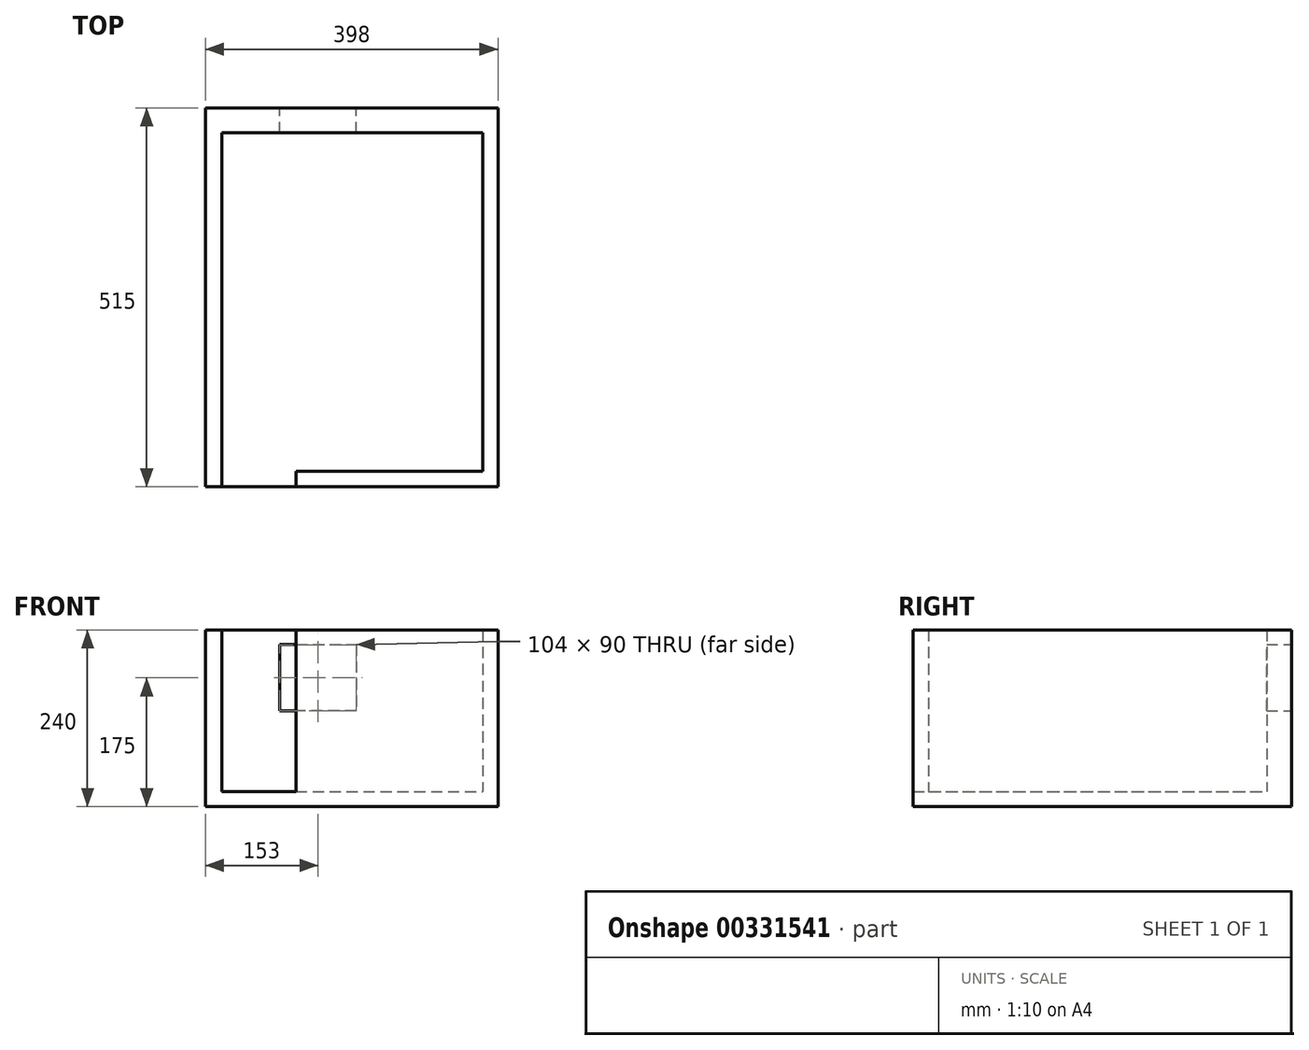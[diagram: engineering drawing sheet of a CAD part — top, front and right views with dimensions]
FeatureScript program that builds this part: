
annotation { "Feature Type Name" : "Feature", "Feature Type Description" : "" }
export const myFeature = defineFeature(function(context is Context, id is Id, definition is map)
    precondition{}
    {
        {
            var Q0;
            Q0=qCreatedBy(makeId("Top.planeOp"),FACE);
            var sketch = newSketch(context, id + "F0", { "sketchPlane" : qUnion([Q0])});
            skLineSegment(sketch, "E0", {"start": v(1313, 440) * mm, "end": v(1313, 406) * mm});
            skLineSegment(sketch, "E1", {"start": v(1313, -267) * mm, "end": v(1313, -301) * mm});
            skLineSegment(sketch, "E2", {"start": v(1313, -301) * mm, "end": v(647, -301) * mm});
            skLineSegment(sketch, "E3", {"start": v(1279, -267) * mm, "end": v(647, -267) * mm});
            skLineSegment(sketch, "E4", {"start": v(1279, 406) * mm, "end": v(688, 406) * mm});
            skLineSegment(sketch, "E5", {"start": v(688, 406) * mm, "end": v(688, -75) * mm});
            skLineSegment(sketch, "E6", {"start": v(688, -75) * mm, "end": v(413, -75) * mm});
            skLineSegment(sketch, "E7", {"start": v(647, -301) * mm, "end": v(647, -267) * mm});
            skLineSegment(sketch, "E8", {"start": v(536, -301) * mm, "end": v(536, -267) * mm});
            skLineSegment(sketch, "E9", {"start": v(536, -267) * mm, "end": v(328, -267) * mm});
            skLineSegment(sketch, "E10", {"start": v(328, -267) * mm, "end": v(328, -407) * mm});
            skLineSegment(sketch, "E11", {"start": v(328, -407) * mm, "end": v(-40, -407) * mm});
            skLineSegment(sketch, "E12", {"start": v(-40, -407) * mm, "end": v(-40, -188) * mm});
            skLineSegment(sketch, "E13", {"start": v(-40, -188) * mm, "end": v(-105, -188) * mm});
            skLineSegment(sketch, "E14", {"start": v(536, -301) * mm, "end": v(362, -301) * mm});
            skLineSegment(sketch, "E15", {"start": v(362, -301) * mm, "end": v(362, -440) * mm});
            skLineSegment(sketch, "E16", {"start": v(-60, -407) * mm, "end": v(-60, -215) * mm});
            skLineSegment(sketch, "E17", {"start": v(-60, -215) * mm, "end": v(-105, -215) * mm});
            skLineSegment(sketch, "E18", {"start": v(-105, -188) * mm, "end": v(-105, -215) * mm});
            skLineSegment(sketch, "E19", {"start": v(-60, -407) * mm, "end": v(-282, -407) * mm});
            skLineSegment(sketch, "E20", {"start": v(-282, -407) * mm, "end": v(-282, -287) * mm});
            skLineSegment(sketch, "E21", {"start": v(-282, -287) * mm, "end": v(-330, -287) * mm});
            skLineSegment(sketch, "E22", {"start": v(-330, -287) * mm, "end": v(-330, -407) * mm});
            skLineSegment(sketch, "E23", {"start": v(-330, -407) * mm, "end": v(-497, -407) * mm});
            skLineSegment(sketch, "E24", {"start": v(-197, -188) * mm, "end": v(-197, -215) * mm});
            skLineSegment(sketch, "E25", {"start": v(-197, -188) * mm, "end": v(-765, -188) * mm});
            skLineSegment(sketch, "E26", {"start": v(-197, -215) * mm, "end": v(-497, -215) * mm});
            skLineSegment(sketch, "E27", {"start": v(-497, -215) * mm, "end": v(-497, -231) * mm});
            skLineSegment(sketch, "E28", {"start": v(-497, -231) * mm, "end": v(-497, -293) * mm});
            skLineSegment(sketch, "E29", {"start": v(-497, -407) * mm, "end": v(-497, -349) * mm});
            skLineSegment(sketch, "E30", {"start": v(413, -75) * mm, "end": v(413, -54) * mm});
            skLineSegment(sketch, "E31", {"start": v(413, -54) * mm, "end": v(667, -54) * mm});
            skLineSegment(sketch, "E32", {"start": v(667, -54) * mm, "end": v(667, 406) * mm});
            skLineSegment(sketch, "E33", {"start": v(667, 406) * mm, "end": v(495, 406) * mm});
            skLineSegment(sketch, "E34", {"start": v(312, 406) * mm, "end": v(391, 406) * mm});
            skLineSegment(sketch, "E35", {"start": v(391, 406) * mm, "end": v(391, 440) * mm});
            skLineSegment(sketch, "E36", {"start": v(495, 406) * mm, "end": v(495, 440) * mm});
            skLineSegment(sketch, "E37", {"start": v(1313, 440) * mm, "end": v(495, 440) * mm});
            skLineSegment(sketch, "E38", {"start": v(312, -75) * mm, "end": v(60, -75) * mm});
            skLineSegment(sketch, "E39", {"start": v(-1279, 406) * mm, "end": v(-1279, 7) * mm});
            skLineSegment(sketch, "E40", {"start": v(-790, 406) * mm, "end": v(-790, 7) * mm});
            skLineSegment(sketch, "E41", {"start": v(-1279, 7) * mm, "end": v(-910, 7) * mm});
            skLineSegment(sketch, "E42", {"start": v(-790, 7) * mm, "end": v(-808, 7) * mm});
            skLineSegment(sketch, "E43", {"start": v(-765, -188) * mm, "end": v(-765, -208) * mm});
            skLineSegment(sketch, "E44", {"start": v(290, 141) * mm, "end": v(290, 406) * mm});
            skLineSegment(sketch, "E45", {"start": v(290, 141) * mm, "end": v(75, 141) * mm});
            skLineSegment(sketch, "E46", {"start": v(75, -46) * mm, "end": v(75, 141) * mm});
            skLineSegment(sketch, "E47", {"start": v(60, -75) * mm, "end": v(60, -46) * mm});
            skLineSegment(sketch, "E48", {"start": v(391, 406) * mm, "end": v(312, 406) * mm});
            skLineSegment(sketch, "E49", {"start": v(-139, 406) * mm, "end": v(-139, 440) * mm});
            skLineSegment(sketch, "E50", {"start": v(-318, 406) * mm, "end": v(-318, 440) * mm});
            skLineSegment(sketch, "E51", {"start": v(-515, 406) * mm, "end": v(-515, 440) * mm});
            skLineSegment(sketch, "E52", {"start": v(-694, 406) * mm, "end": v(-694, 440) * mm});
            skLineSegment(sketch, "E53", {"start": v(-770, 406) * mm, "end": v(-770, 9) * mm});
            skLineSegment(sketch, "E54", {"start": v(-694, 406) * mm, "end": v(-770, 406) * mm});
            skLineSegment(sketch, "E55", {"start": v(75, 406) * mm, "end": v(-139, 406) * mm});
            skLineSegment(sketch, "E56", {"start": v(-318, 406) * mm, "end": v(-515, 406) * mm});
            skLineSegment(sketch, "E57", {"start": v(-318, 440) * mm, "end": v(-515, 440) * mm});
            skLineSegment(sketch, "E58", {"start": v(-770, 9) * mm, "end": v(-754, 9) * mm});
            skLineSegment(sketch, "E59", {"start": v(-677, 9) * mm, "end": v(-659, 9) * mm});
            skLineSegment(sketch, "E60", {"start": v(-659, 9) * mm, "end": v(-659, -5) * mm});
            skLineSegment(sketch, "E61", {"start": v(-659, -5) * mm, "end": v(-659, -46) * mm});
            skLineSegment(sketch, "E62", {"start": v(-659, -46) * mm, "end": v(-60, -46) * mm});
            skLineSegment(sketch, "E63", {"start": v(-60, -75) * mm, "end": v(-60, -46) * mm});
            skLineSegment(sketch, "E64", {"start": v(60, -75) * mm, "end": v(128, -75) * mm});
            skLineSegment(sketch, "E65", {"start": v(60, -46) * mm, "end": v(75, -46) * mm});
            skLineSegment(sketch, "E66", {"start": v(96, -46) * mm, "end": v(290, -46) * mm});
            skLineSegment(sketch, "E67", {"start": v(-60, -75) * mm, "end": v(-677, -75) * mm});
            skLineSegment(sketch, "E68", {"start": v(-677, 9) * mm, "end": v(-677, -75) * mm});
            skLineSegment(sketch, "E69", {"start": v(-754, 9) * mm, "end": v(-754, -13) * mm});
            skLineSegment(sketch, "E70", {"start": v(-808, 7) * mm, "end": v(-808, -13) * mm});
            skLineSegment(sketch, "E71", {"start": v(-808, -13) * mm, "end": v(-754, -13) * mm});
            skLineSegment(sketch, "E72", {"start": v(-910, 7) * mm, "end": v(-910, -29) * mm});
            skLineSegment(sketch, "E73", {"start": v(-1279, -406) * mm, "end": v(-935, -406) * mm});
            skLineSegment(sketch, "E74", {"start": v(-1313, -440) * mm, "end": v(-935, -440) * mm});
            skLineSegment(sketch, "E75", {"start": v(-910, -29) * mm, "end": v(-935, -29) * mm});
            skLineSegment(sketch, "E76", {"start": v(-935, -13) * mm, "end": v(-1279, -13) * mm});
            skLineSegment(sketch, "E77", {"start": v(-910, -132) * mm, "end": v(-935, -132) * mm});
            skLineSegment(sketch, "E78", {"start": v(-910, -29) * mm, "end": v(-910, -13) * mm});
            skLineSegment(sketch, "E79", {"start": v(-935, -406) * mm, "end": v(-935, -132) * mm});
            skLineSegment(sketch, "E80", {"start": v(-935, -29) * mm, "end": v(-935, -13) * mm});
            skLineSegment(sketch, "E81", {"start": v(-877, -208) * mm, "end": v(-877, -188) * mm});
            skLineSegment(sketch, "E82", {"start": v(-910, -132) * mm, "end": v(-910, -188) * mm});
            skLineSegment(sketch, "E83", {"start": v(-877, -188) * mm, "end": v(-910, -188) * mm});
            skLineSegment(sketch, "E84", {"start": v(-877, -208) * mm, "end": v(-904, -208) * mm});
            skLineSegment(sketch, "E85", {"start": v(-904, -208) * mm, "end": v(-904, -406) * mm});
            skLineSegment(sketch, "E86", {"start": v(-904, -406) * mm, "end": v(-648, -406) * mm});
            skLineSegment(sketch, "E87", {"start": v(-765, -208) * mm, "end": v(-648, -208) * mm});
            skLineSegment(sketch, "E88", {"start": v(-648, -208) * mm, "end": v(-648, -273) * mm});
            skLineSegment(sketch, "E89", {"start": v(-648, -406) * mm, "end": v(-648, -343) * mm});
            skLineSegment(sketch, "E90", {"start": v(-935, -440) * mm, "end": v(362, -440) * mm});
            skLineSegment(sketch, "E91", {"start": v(151, 406) * mm, "end": v(151, 440) * mm});
            skLineSegment(sketch, "E92", {"start": v(224, 406) * mm, "end": v(224, 440) * mm});
            skLineSegment(sketch, "E93", {"start": v(290, 406) * mm, "end": v(224, 406) * mm});
            skLineSegment(sketch, "E94", {"start": v(151, 406) * mm, "end": v(96, 406) * mm});
            skLineSegment(sketch, "E95", {"start": v(391, 440) * mm, "end": v(224, 440) * mm});
            skLineSegment(sketch, "E96", {"start": v(151, 440) * mm, "end": v(-139, 440) * mm});
            skLineSegment(sketch, "E97", {"start": v(-907, 406) * mm, "end": v(-907, 440) * mm});
            skLineSegment(sketch, "E98", {"start": v(-1085, 406) * mm, "end": v(-1085, 440) * mm});
            skLineSegment(sketch, "E99", {"start": v(-790, 406) * mm, "end": v(-907, 406) * mm});
            skLineSegment(sketch, "E100", {"start": v(-1085, 406) * mm, "end": v(-1279, 406) * mm});
            skLineSegment(sketch, "E101", {"start": v(-694, 440) * mm, "end": v(-907, 440) * mm});
            skLineSegment(sketch, "E102", {"start": v(-1085, 440) * mm, "end": v(-1313, 440) * mm});
            skLineSegment(sketch, "E103", {"start": v(-1279, -118) * mm, "end": v(-1313, -118) * mm});
            skLineSegment(sketch, "E104", {"start": v(-1279, -297) * mm, "end": v(-1313, -297) * mm});
            skLineSegment(sketch, "E105", {"start": v(-1279, -13) * mm, "end": v(-1279, -118) * mm});
            skLineSegment(sketch, "E106", {"start": v(-1279, -297) * mm, "end": v(-1279, -406) * mm});
            skLineSegment(sketch, "E107", {"start": v(-1313, 440) * mm, "end": v(-1313, -118) * mm});
            skLineSegment(sketch, "E108", {"start": v(-1313, -297) * mm, "end": v(-1313, -440) * mm});
            skLineSegment(sketch, "E109", {"start": v(-648, -273) * mm, "end": v(-630, -273) * mm});
            skLineSegment(sketch, "E110", {"start": v(-648, -343) * mm, "end": v(-630, -343) * mm});
            skLineSegment(sketch, "E111", {"start": v(-515, -349) * mm, "end": v(-497, -349) * mm});
            skLineSegment(sketch, "E112", {"start": v(-515, -293) * mm, "end": v(-497, -293) * mm});
            skLineSegment(sketch, "E113", {"start": v(-515, -349) * mm, "end": v(-515, -406) * mm});
            skLineSegment(sketch, "E114", {"start": v(-630, -343) * mm, "end": v(-630, -406) * mm});
            skLineSegment(sketch, "E115", {"start": v(-630, -406) * mm, "end": v(-515, -406) * mm});
            skLineSegment(sketch, "E116", {"start": v(-630, -273) * mm, "end": v(-630, -206) * mm});
            skLineSegment(sketch, "E117", {"start": v(-630, -206) * mm, "end": v(-515, -206) * mm});
            skLineSegment(sketch, "E118", {"start": v(-515, -293) * mm, "end": v(-515, -206) * mm});
            skLineSegment(sketch, "E119", {"start": v(290, 43) * mm, "end": v(312, 43) * mm});
            skLineSegment(sketch, "E120", {"start": v(290, 124) * mm, "end": v(312, 124) * mm});
            skLineSegment(sketch, "E121", {"start": v(312, -75) * mm, "end": v(312, 43) * mm});
            skLineSegment(sketch, "E122", {"start": v(312, 124) * mm, "end": v(312, 406) * mm});
            skLineSegment(sketch, "E123", {"start": v(290, -46) * mm, "end": v(290, 43) * mm});
            skLineSegment(sketch, "E124", {"start": v(96, 222) * mm, "end": v(75, 222) * mm});
            skLineSegment(sketch, "E125", {"start": v(96, 222) * mm, "end": v(96, 406) * mm});
            skLineSegment(sketch, "E126", {"start": v(75, 222) * mm, "end": v(75, 406) * mm});
            skLineSegment(sketch, "E127", {"start": v(96, -46) * mm, "end": v(96, 124) * mm});
            skLineSegment(sketch, "E128", {"start": v(290, 124) * mm, "end": v(96, 124) * mm});
            skLineSegment(sketch, "E129", {"start": v(1279, -219) * mm, "end": v(1313, -219) * mm});
            skLineSegment(sketch, "E130", {"start": v(1279, -26) * mm, "end": v(1313, -26) * mm});
            skLineSegment(sketch, "E131", {"start": v(1279, 46) * mm, "end": v(1313, 46) * mm});
            skLineSegment(sketch, "E132", {"start": v(1279, 239) * mm, "end": v(1313, 239) * mm});
            skLineSegment(sketch, "E133", {"start": v(1313, 406) * mm, "end": v(1313, 239) * mm});
            skLineSegment(sketch, "E134", {"start": v(1279, 406) * mm, "end": v(1279, 239) * mm});
            skLineSegment(sketch, "E135", {"start": v(1313, 46) * mm, "end": v(1313, -26) * mm});
            skLineSegment(sketch, "E136", {"start": v(1313, -219) * mm, "end": v(1313, -267) * mm});
            skLineSegment(sketch, "E137", {"start": v(1279, 46) * mm, "end": v(1279, -26) * mm});
            skLineSegment(sketch, "E138", {"start": v(1279, -219) * mm, "end": v(1279, -267) * mm});
            skLineSegment(sketch, "E139", {"start": v(1313, -301) * mm, "end": v(1313, 440) * mm});
            skLineSegment(sketch, "E140", {"start": v(1313, -301) * mm, "end": v(362, -301) * mm});
            skLineSegment(sketch, "E141", {"start": v(362, -440) * mm, "end": v(-1313, -440) * mm});
            skLineSegment(sketch, "E142", {"start": v(-1313, 440) * mm, "end": v(-1313, -440) * mm});
            skLineSegment(sketch, "E143", {"start": v(-1313, 440) * mm, "end": v(1313, 440) * mm});
            skLineSegment(sketch, "E144", {"start": v(-321.5, -37.21) * mm, "end": v(-321.5, 162.79) * mm});
            skLineSegment(sketch, "E145", {"start": v(-321.5, -37.21) * mm, "end": v(-511.5, -37.21) * mm});
            skLineSegment(sketch, "E146", {"start": v(-321.5, 162.79) * mm, "end": v(-511.5, 162.79) * mm});
            skLineSegment(sketch, "E147", {"start": v(-511.5, -37.21) * mm, "end": v(-511.5, 162.79) * mm});
            skLineSegment(sketch, "E148", {"start": v(-321.5, -29.2) * mm, "end": v(-511.5, -29.2) * mm});
            skLineSegment(sketch, "E149", {"start": v(-499.08, -21.75) * mm, "end": v(-430.85, -21.75) * mm});
            skLineSegment(sketch, "E150", {"start": v(-430.85, -21.75) * mm, "end": v(-430.85, 2.94) * mm});
            skLineSegment(sketch, "E151", {"start": v(-430.85, 2.94) * mm, "end": v(-499.08, 2.94) * mm});
            skLineSegment(sketch, "E152", {"start": v(-499.08, 2.94) * mm, "end": v(-499.08, -21.75) * mm});
            skLineSegment(sketch, "E153", {"start": v(-333.92, -21.75) * mm, "end": v(-402.15, -21.75) * mm});
            skLineSegment(sketch, "E154", {"start": v(-402.15, -21.75) * mm, "end": v(-402.15, 2.94) * mm});
            skLineSegment(sketch, "E155", {"start": v(-402.15, 2.94) * mm, "end": v(-333.92, 2.94) * mm});
            skLineSegment(sketch, "E156", {"start": v(-333.92, 2.94) * mm, "end": v(-333.92, -21.75) * mm});
            skLineSegment(sketch, "E157", {"start": v(-321.5, 13.1) * mm, "end": v(-416.5, 13.1) * mm});
            skLineSegment(sketch, "E158", {"start": v(-511.5, 36.6) * mm, "end": v(-491.94, 63.04) * mm});
            skLineSegment(sketch, "E159", {"start": v(-491.94, 63.04) * mm, "end": v(-416.5, 13.1) * mm});
            skLineSegment(sketch, "E160", {"start": v(-416.5, 13.1) * mm, "end": v(-511.5, 36.6) * mm});
            skLineSegment(sketch, "E161", {"start": v(-321.5, 159.23) * mm, "end": v(-511.5, 159.23) * mm});
            skLineSegment(sketch, "E162", {"start": v(-552.43, 3.31) * mm, "end": v(-520.43, 3.31) * mm});
            skLineSegment(sketch, "E163", {"start": v(-552.43, 3.31) * mm, "end": v(-552.43, -36.7) * mm});
            skLineSegment(sketch, "E164", {"start": v(-520.43, 3.31) * mm, "end": v(-520.43, -36.7) * mm});
            skLineSegment(sketch, "E165", {"start": v(-552.43, -36.7) * mm, "end": v(-520.43, -36.7) * mm});
            skLineSegment(sketch, "E166", {"start": v(-552.43, -6.69) * mm, "end": v(-520.43, -6.69) * mm});
            skLineSegment(sketch, "E167", {"start": v(-552.43, -3.69) * mm, "end": v(-520.43, -3.69) * mm});
            skLineSegment(sketch, "E168", {"start": v(-552.43, -0.69) * mm, "end": v(-520.43, -0.69) * mm});
            skLineSegment(sketch, "E169", {"start": v(-552.43, 2.31) * mm, "end": v(-520.43, 2.31) * mm});
            skLineSegment(sketch, "E170", {"start": v(-280.57, 3.31) * mm, "end": v(-312.57, 3.31) * mm});
            skLineSegment(sketch, "E171", {"start": v(-280.57, 3.31) * mm, "end": v(-280.57, -36.7) * mm});
            skLineSegment(sketch, "E172", {"start": v(-312.57, 3.31) * mm, "end": v(-312.57, -36.7) * mm});
            skLineSegment(sketch, "E173", {"start": v(-280.57, -36.7) * mm, "end": v(-312.57, -36.7) * mm});
            skLineSegment(sketch, "E174", {"start": v(-280.57, -6.69) * mm, "end": v(-312.57, -6.69) * mm});
            skLineSegment(sketch, "E175", {"start": v(-280.57, -3.69) * mm, "end": v(-312.57, -3.69) * mm});
            skLineSegment(sketch, "E176", {"start": v(-280.57, -0.69) * mm, "end": v(-312.57, -0.69) * mm});
            skLineSegment(sketch, "E177", {"start": v(-280.57, 2.31) * mm, "end": v(-312.57, 2.31) * mm});
            skLineSegment(sketch, "E178", {"start": v(-765, 395.6) * mm, "end": v(-765, 20.6) * mm});
            skLineSegment(sketch, "E179", {"start": v(-765, 395.6) * mm, "end": v(-705, 395.6) * mm});
            skLineSegment(sketch, "E180", {"start": v(-705, 395.6) * mm, "end": v(-705, 20.6) * mm});
            skLineSegment(sketch, "E181", {"start": v(-765, 20.6) * mm, "end": v(-705, 20.6) * mm});
            skLineSegment(sketch, "E182", {"start": v(-705, 395.6) * mm, "end": v(-700, 395.6) * mm});
            skLineSegment(sketch, "E183", {"start": v(-700, 395.6) * mm, "end": v(-700, 20.6) * mm});
            skLineSegment(sketch, "E184", {"start": v(-705, 20.6) * mm, "end": v(-700, 20.6) * mm});
            skLineSegment(sketch, "E185", {"start": v(-705, 114.35) * mm, "end": v(-700, 114.35) * mm});
            skLineSegment(sketch, "E186", {"start": v(-705, 301.85) * mm, "end": v(-700, 301.85) * mm});
            skLineSegment(sketch, "E187", {"start": v(-705, 208.1) * mm, "end": v(-700, 208.1) * mm});
            skLineSegment(sketch, "E188", {"start": v(-705, 348.73) * mm, "end": v(-700, 348.73) * mm});
            skLineSegment(sketch, "E189", {"start": v(-705, 67.47) * mm, "end": v(-700, 67.47) * mm});
            skSolve(sketch);
        }
        {
            var Q0;
            Q0=makeQuery(id+"F0.imprint","IMPRINT",FACE,{"disambiguationData":[TD([[makeQuery(id+"F0.imprint","IMPRINT",EDGE,{"derivedFrom":sQuery(id+"F0.wireOp",EDGE,"E3")}),-1.0]])]});
            var sketch = newSketch(context, id + "F1", { "sketchPlane" : qUnion([Q0])});
            skLineSegment(sketch, "E190.0", {"start": v(688, -75) * mm, "end": v(413, -75) * mm});
            skLineSegment(sketch, "E191.0", {"start": v(290, 141) * mm, "end": v(290, 406) * mm});
            skLineSegment(sketch, "E192.0", {"start": v(290, 440) * mm, "end": v(688, 440) * mm});
            skLineSegment(sketch, "E193.bottom", {"start": v(688, -75) * mm, "end": v(290, -75) * mm});
            skLineSegment(sketch, "E193.top", {"start": v(688, 440) * mm, "end": v(290, 440) * mm});
            skLineSegment(sketch, "E193.left", {"start": v(688, -75) * mm, "end": v(688, 440) * mm});
            skLineSegment(sketch, "E193.right", {"start": v(290, -75) * mm, "end": v(290, 440) * mm});
            skPoint(sketch, "E194.orphan", {"position": v(-1313, 440) * mm});
            skPoint(sketch, "E195.orphan", {"position": v(1313, 440) * mm});
            skSolve(sketch);
        }
        {
            var Q0;
            Q0 = qSketchRegion(id + "F1", true);
            extrude(context, id + "F2", {"entities" : qUnion([Q0]), "depth" : 20 * mm});
        }
        {
            var Q0;
            Q0=makeQuery(id+"F2.opExtrude","CAP_FACE",FACE,{"disambiguationData":[OSD([sQuery(id+"F1.wireOp",EDGE,"E193.bottom"),sQuery(id+"F1.wireOp",EDGE,"E193.top"),sQuery(id+"F1.wireOp",EDGE,"E193.left"),sQuery(id+"F1.wireOp",EDGE,"E193.right")])],"isStart":false});
            var sketch = newSketch(context, id + "F3", { "sketchPlane" : qUnion([Q0])});
            skLineSegment(sketch, "E196.0", {"start": v(667, -54) * mm, "end": v(667, 406) * mm});
            skLineSegment(sketch, "E197.0", {"start": v(413, -54) * mm, "end": v(667, -54) * mm});
            skLineSegment(sketch, "E198.0", {"start": v(688, -75) * mm, "end": v(413, -75) * mm});
            skLineSegment(sketch, "E199.0", {"start": v(688, 406) * mm, "end": v(688, -75) * mm});
            skLineSegment(sketch, "E200.0", {"start": v(413, -75) * mm, "end": v(413, -54) * mm});
            skLineSegment(sketch, "E201.0", {"start": v(312, -75) * mm, "end": v(312, 43) * mm});
            skLineSegment(sketch, "E202.0", {"start": v(312, 124) * mm, "end": v(312, 406) * mm});
            skLineSegment(sketch, "E203.0", {"start": v(290, -75) * mm, "end": v(290, 440) * mm});
            skLineSegment(sketch, "E204.0", {"start": v(-1313, 440) * mm, "end": v(1313, 440) * mm});
            skLineSegment(sketch, "E205", {"start": v(312, 43) * mm, "end": v(312, 124) * mm});
            skLineSegment(sketch, "E206", {"start": v(312, 406) * mm, "end": v(667, 406) * mm});
            skLineSegment(sketch, "E207", {"start": v(688, 440) * mm, "end": v(688, 406) * mm});
            skLineSegment(sketch, "E208", {"start": v(290, -75) * mm, "end": v(312, -75) * mm});
            skSolve(sketch);
        }
        {
            var Q0;
            Q0 = qSketchRegion(id + "F3", true);
            extrude(context, id + "F4", {"entities" : qUnion([Q0]), "operationType" : NewBodyOperationType.ADD, "depth" : 220 * mm});
        }
        {
            var Q0;
            Q0=makeQuery(id+"F4.boolean.opBoolean","MERGE",FACE,{"derivedFrom":[makeQuery(id+"F2.opExtrude","SWEPT_FACE",FACE,{"disambiguationData":[OSD([sQuery(id+"F1.wireOp",EDGE,"E193.top")])]}),makeQuery(id+"F4.opExtrude","SWEPT_FACE",FACE,{"disambiguationData":[OSD([sQuery(id+"F3.wireOp",EDGE,"E204.0")])]})]});
            var sketch = newSketch(context, id + "F5", { "sketchPlane" : qUnion([Q0])});
            skLineSegment(sketch, "E209.0", {"start": v(-312, 0) * mm, "end": v(-391, 0) * mm, "construction": true});
            skLineSegment(sketch, "E210.0", {"start": v(-667, 0) * mm, "end": v(-495, 0) * mm, "construction": true});
            skLineSegment(sketch, "E211", {"start": v(-391, 220) * mm, "end": v(-495, 220) * mm});
            skLineSegment(sketch, "E212", {"start": v(-495, 220) * mm, "end": v(-495, 130) * mm});
            skLineSegment(sketch, "E213", {"start": v(-495, 130) * mm, "end": v(-391, 130) * mm});
            skLineSegment(sketch, "E214", {"start": v(-391, 130) * mm, "end": v(-391, 220) * mm});
            skSolve(sketch);
        }
        {
            var Q0;
            Q0 = qSketchRegion(id + "F5", true);
            extrude(context, id + "F6", {"entities" : qUnion([Q0]), "operationType" : NewBodyOperationType.REMOVE, "oppositeDirection" : true, "depth" : 40 * mm});
        }
    });
